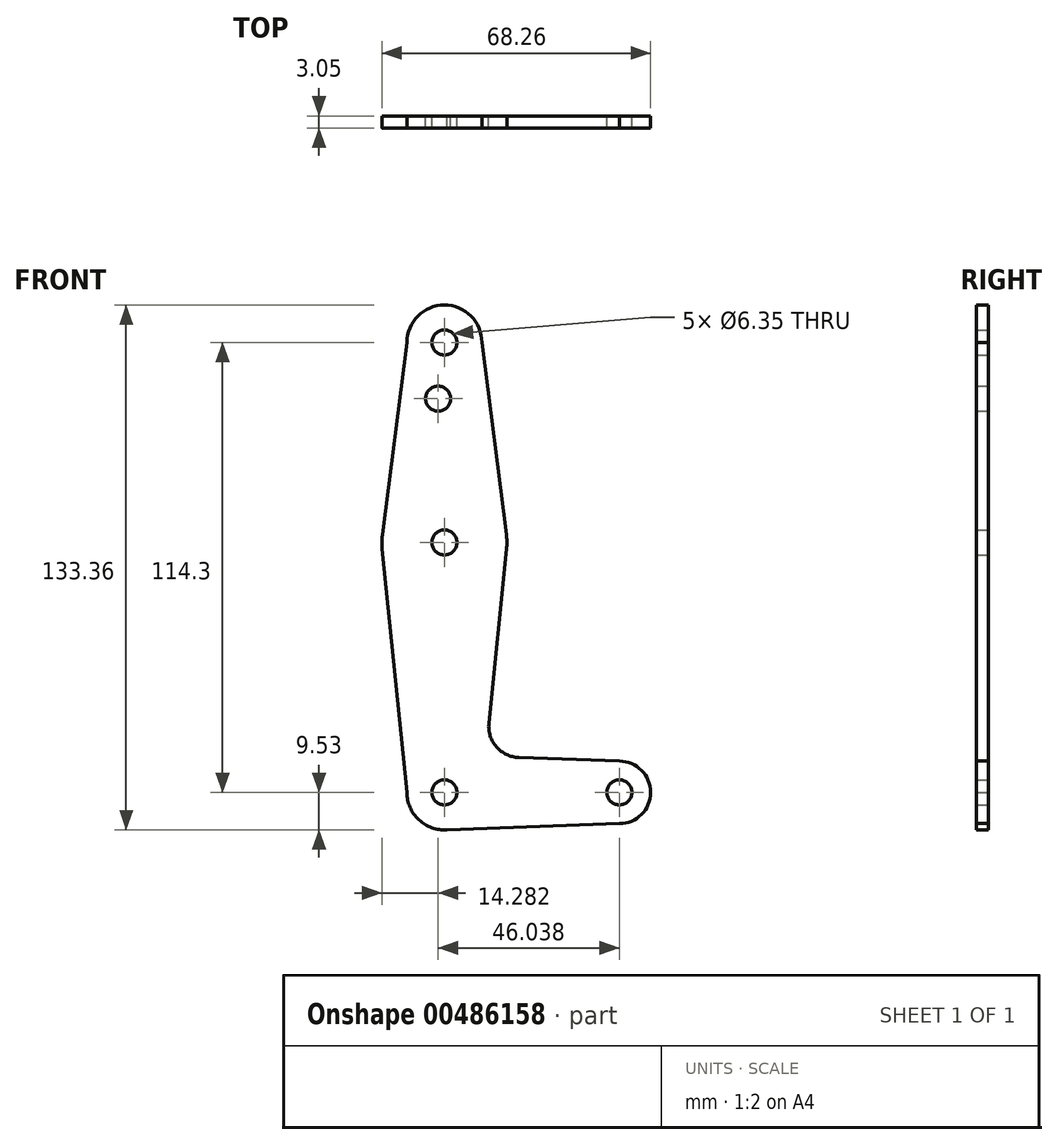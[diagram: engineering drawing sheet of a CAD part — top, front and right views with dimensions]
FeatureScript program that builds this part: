
annotation { "Feature Type Name" : "Feature", "Feature Type Description" : "" }
export const myFeature = defineFeature(function(context is Context, id is Id, definition is map)
    precondition{}
    {
        {
            var Q0;
            Q0=qCreatedBy(makeId("Front.planeOp"),FACE);
            var sketch = newSketch(context, id + "F0", { "sketchPlane" : qUnion([Q0])});
            skLineSegment(sketch, "E0", {"start": v(0, 0) * mm, "end": v(0, 114.3) * mm, "construction": true});
            skLineSegment(sketch, "E1", {"start": v(0, 0) * mm, "end": v(44.45, 0) * mm, "construction": true});
            skCircle(sketch, "E2", {"center": v(0, 114.3) * mm, "radius": 9.53 * mm});
            skCircle(sketch, "E3", {"center": v(0, 63.5) * mm, "radius": 15.88 * mm});
            skCircle(sketch, "E4", {"center": v(0, 0) * mm, "radius": 9.53 * mm});
            skCircle(sketch, "E5", {"center": v(44.45, 0) * mm, "radius": 7.94 * mm});
            skLineSegment(sketch, "E6", {"start": v(9.53, 114.3) * mm, "end": v(15.75, 65.5) * mm});
            skLineSegment(sketch, "E7", {"start": v(-9.53, 114.3) * mm, "end": v(-15.75, 65.5) * mm});
            skLineSegment(sketch, "E8", {"start": v(11.3, 17.6) * mm, "end": v(15.8, 61.9) * mm});
            skLineSegment(sketch, "E9", {"start": v(-15.8, 61.9) * mm, "end": v(-9.52, 0) * mm});
            skLineSegment(sketch, "E10", {"start": v(44.45, 7.94) * mm, "end": v(18.93, 8.85) * mm});
            skLineSegment(sketch, "E11", {"start": v(0, -9.52) * mm, "end": v(44.45, -7.94) * mm});
            skCircle(sketch, "E12", {"center": v(0, 114.3) * mm, "radius": 3.18 * mm});
            skCircle(sketch, "E13", {"center": v(0, 63.5) * mm, "radius": 3.18 * mm});
            skCircle(sketch, "E14", {"center": v(0, 0) * mm, "radius": 3.18 * mm});
            skCircle(sketch, "E15", {"center": v(44.45, 0) * mm, "radius": 3.18 * mm});
            skCircle(sketch, "E16", {"center": v(-1.59, 100.03) * mm, "radius": 3.18 * mm});
            skArc(sketch, "E17.filletArc", {"start": v(11.3, 17.6) * mm, "mid": v(13.22, 11.57) * mm, "end": v(18.93, 8.85) * mm});
            skSolve(sketch);
        }
        {
            var Q0;
            Q0 = qSketchRegion(id + "F0", true);
            extrude(context, id + "F1", {"entities" : qUnion([Q0]), "depth" : 3.05 * mm});
        }
    });
